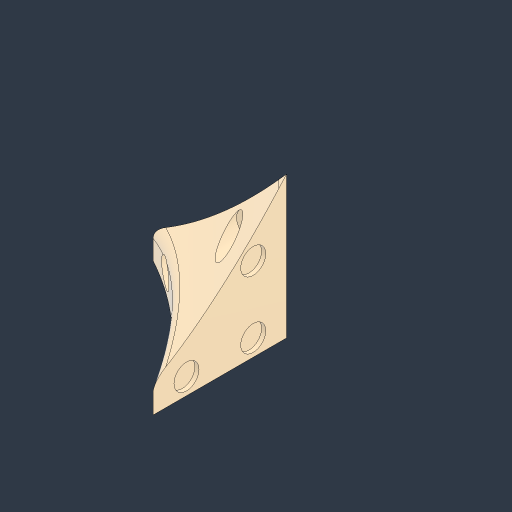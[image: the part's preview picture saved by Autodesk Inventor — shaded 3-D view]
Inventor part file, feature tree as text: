
AUTODESK INVENTOR PART (.ipt)
format: ipt  version: 2024.3 (Build 283343000, 343)  size: 278,016 bytes
history: native  units: in
note: dims shown in document units (in); Inventor stores cm internally (conversion verified against a paired STEP export)
features: sketch x9, projected_geometry x7, extrude x3, other x3, loft x2, hole x2, fillet x1, plane x1
ambient origin geometry x8: Origin, YZ Plane, XZ Plane, XY Plane, X Axis, Y Axis, Z Axis, Center Point
bodies: Solid1 (feature_tree)
feature tree (28):
  extrude  "Extrusion1"  Depth=2.0in
  loft  "Loft1"
  loft  "Loft2"
  extrude  "Extrusion2"  TaperAngle=0.0deg  [1 undecoded]
  hole  "Hole1"  [1 undecoded]
  fillet  "Fillet1"  [1 undecoded]
  plane  "Work Plane1"
  extrude  "Extrusion3"  Depth=0.75in TaperAngle=0.0deg
  hole  "Hole2"  [1 undecoded]
  sketch  "Sketch1"  dims[d0=2.0in d1=2.0in]
  sketch  "Sketch2"  dims[d2=2.0in d3=0.0in d4=-0.0984in d5=1.1811in]
  other  "2D Equation Curve1"
  projected_geometry  "Projected Loop1"
  sketch  "Sketch3"  dims[d6=0.5in d7=-0.0984in d8=1.1811in]
  other  "2D Equation Curve2"
  projected_geometry  "Projected Loop2"
  sketch  "Sketch4"  dims[d9=0.5in d10=0.0in d11=90.0deg]
  projected_geometry  "Projected Loop3"
  sketch  "Sketch5"  dims[d12=0.0in d13=90.0deg d14=0.0in d15=90.0deg d16=0.0in d17=90.0deg]
  projected_geometry  "Projected Loop4"
  other  "Edges1"
  sketch  "Sketch6"  dims[d18=0.0in d19=90.0deg d20=0.75in d21=0.0in]
  projected_geometry  "Projected Loop5"
  sketch  "Sketch7"  dims[d22=0.25in d23=0.5in]
  projected_geometry  "Projected Loop6"
  sketch  "Sketch8"  dims[d24=1.0in]
  sketch  "Sketch9"  dims[d25=1.0in d26=0.201in d27=0.75in d28=0.385in d29=0.25in d30=0.5635in d31=1.0in d32=0.8108in d33=5.0in d34=0.25in d35=90.0deg d36=0.375in d37=0.375in d38=0.375in d39=1.9375in d40=0.0in d41=0.25in d42=1.0in d43=1.0in d44=0.5in d45=0.375in d46=0.75in d47=0.375in d48=0.25in d49=0.5635in d50=0.0625in d51=0.0in]
  projected_geometry  "Projected Loop7"
note: 4 required parameter values undecoded (feature->parameter linkage not recoverable at this tier; creation-order binding heuristic only, values carry confidence <= 0.55)
